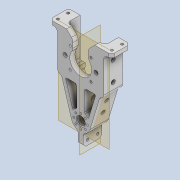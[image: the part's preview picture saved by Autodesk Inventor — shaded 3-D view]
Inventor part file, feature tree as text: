
AUTODESK INVENTOR PART (.ipt)
format: ipt  version: 2020 (Build 240168000, 168)  size: 733,696 bytes
history: native  units: mm
features: extrude x21, sketch x21, projected_geometry x17, fillet x15, thicken_offset x6, chamfer x5, mirror x4, other x4, plane x2, pattern_circular x2, reference x2
ambient origin geometry x8: Origin, YZ Plane, XZ Plane, XY Plane, X Axis, Y Axis, Z Axis, Center Point
bodies: Solid1 (feature_tree)
feature tree (99):
  extrude  "Extrusion1"  Depth=15.0mm
  extrude  "Extrusion2"  Depth=30.0mm
  extrude  "Extrusion3"  Depth=6.0mm
  extrude  "Extrusion4"  Depth=4.0mm TaperAngle=0.0deg
  extrude  "Extrusion5"  Depth=4.0mm TaperAngle=0.0deg
  extrude  "Extrusion6"  Depth=3.0mm
  extrude  "Extrusion7"  Depth=4.0mm
  plane  "Work Plane1"
  extrude  "Extrusion8"  Depth=4.0mm
  chamfer  "Chamfer1"  Distance=10.5mm
  extrude  "Extrusion9"  Depth=30.0mm
  pattern_circular  "Circular Pattern1"  Count=2  [1 undecoded]
  thicken_offset  "Thicken1"
  fillet  "Fillet1"  Radius=80.0mm
  fillet  "Fillet2"  Radius=4.0mm
  extrude  "Extrusion10"  Depth=5.0mm
  pattern_circular  "Circular Pattern2"  [2 undecoded]
  extrude  "Extrusion11"  Depth=3.0mm
  extrude  "Extrusion12"  Depth=10.0mm TaperAngle=0.0deg
  extrude  "Extrusion13"  Depth=3.0mm TaperAngle=360.0deg
  extrude  "Extrusion14"  Depth=10.0mm TaperAngle=0.0deg
  extrude  "Extrusion15"  Depth=3.0mm
  plane  "Work Plane2"
  mirror  "Mirror1"
  extrude  "Extrusion16"  Depth=3.0mm
  extrude  "Extrusion17"  Depth=10.0mm TaperAngle=0.0deg
  mirror  "Mirror2"
  extrude  "Extrusion18"  Depth=3.0mm
  mirror  "Mirror3"
  extrude  "Extrusion19"  Depth=3.0mm
  thicken_offset  "Thicken2"
  extrude  "Extrusion20"  Depth=3.0mm
  fillet  "Fillet3"  Radius=10.0mm
  fillet  "Fillet4"  Radius=6.0mm
  fillet  "Fillet5"  Radius=7.0mm
  fillet  "Fillet6"  Radius=5.0mm
  fillet  "Fillet7"  Radius=10.0mm
  fillet  "Fillet8"  Radius=10.0mm
  chamfer  "Chamfer2"  Distance=10.0mm
  fillet  "Fillet9"  Radius=3.2mm
  thicken_offset  "Thicken3"
  thicken_offset  "Thicken4"
  fillet  "Fillet10"  Radius=3.2mm
  fillet  "Fillet11"  Radius=10.0mm
  fillet  "Fillet12"  Radius=6.0mm
  fillet  "Fillet13"  Radius=14.5mm
  chamfer  "Chamfer3"  Distance=6.0mm
  fillet  "Fillet14"  Radius=14.5mm
  chamfer  "Chamfer4"  Distance=3.0mm
  fillet  "Fillet15"  Radius=4.0mm
  extrude  "Extrusion21"  Depth=3.0mm
  mirror  "Mirror4"
  thicken_offset  "Thicken5"
  thicken_offset  "Thicken6"
  chamfer  "Chamfer5"  Distance=2.0mm
  sketch  "Sketch1"  dims[d0=38.7mm d1=15.0mm]
  reference  "Reference1"
  sketch  "Sketch2"  dims[d2=30.0mm d3=30.0mm]
  sketch  "Sketch3"  dims[d4=19.35mm d5=6.0mm]
  projected_geometry  "Projected Loop1"
  sketch  "Sketch4"  dims[d6=38.7mm d7=4.0mm d8=0.0mm]
  projected_geometry  "Projected Loop2"
  sketch  "Sketch5"  dims[d9=17.0mm d10=4.0mm d11=0.0mm]
  projected_geometry  "Projected Loop3"
  sketch  "Sketch6"  dims[d12=3.0mm d13=3.0mm]
  projected_geometry  "Projected Loop4"
  sketch  "Sketch7"  dims[d14=4.0mm d15=0.0mm d16=4.0mm]
  projected_geometry  "Projected Loop5"
  sketch  "Sketch8"  dims[d17=5.0mm d18=4.0mm]
  sketch  "Sketch9"  dims[d19=5.0mm d20=10.5mm d21=0.0mm]
  projected_geometry  "Projected Loop6"
  sketch  "Sketch10"  dims[d22=14.5mm d23=30.0mm]
  projected_geometry  "Projected Loop7"
  sketch  "Sketch11"  dims[d24=3.0mm d25=0.0mm]
  projected_geometry  "Projected Loop8"
  sketch  "Sketch12"  dims[d26=3.0mm d27=0.0mm]
  reference  "Reference2"
  sketch  "Sketch13"  dims[d28=6.15mm]
  projected_geometry  "Projected Loop9"
  sketch  "Sketch14"  dims[d29=3.0mm d30=0.0mm]
  projected_geometry  "Projected Loop10"
  sketch  "Sketch15"  dims[d31=-2.5mm]
  projected_geometry  "Projected Loop11"
  sketch  "Sketch16"  dims[d32=1.0mm]
  projected_geometry  "Projected Loop12"
  projected_geometry  "Projected Loop13"
  sketch  "Sketch17"  dims[d33=9.0mm d34=0.0mm]
  projected_geometry  "Projected Loop14"
  sketch  "Sketch18"  dims[d35=1.0mm d36=2.0mm d37=45.0deg]
  projected_geometry  "Projected Loop15"
  sketch  "Sketch19"  dims[d38=1.5mm d39=20.0mm d40=0.0mm d41=80.0mm d42=360.0deg d44=4.0mm]
  projected_geometry  "Projected Loop16"
  sketch  "Sketch20"  dims[d45=4.0mm d46=5.0mm]
  sketch  "Sketch21"  dims[d47=3.0mm d48=11.5mm d49=1.8mm d50=10.0mm d51=0.0mm d52=40.0mm d53=360.0deg d55=10.0mm d56=0.0mm d57=20.0mm d58=12.0mm d59=10.0mm d60=0.0mm d61=13.0mm d62=4.0mm d63=12.0mm d64=10.0mm d65=0.0mm d66=6.0mm d67=7.0mm d68=5.0mm d69=10.0mm d70=0.0mm d71=10.0mm d72=10.0mm d73=3.2mm d74=3.2mm d75=10.0mm d76=0.0mm d77=6.0mm d78=14.5mm d79=6.0mm d80=14.5mm d81=3.0mm d82=0.0mm d83=4.0mm d84=4.0mm d85=2.0mm d86=2.0mm d87=3.0mm d88=0.0mm d89=7.0mm d90=15.0mm d91=3.2mm d92=3.2mm d93=3.0mm d94=0.0mm d95=4.0mm d96=2.0mm d97=4.0mm d98=2.0mm d99=4.0mm d100=0.0mm d101=2.0mm d102=2.0mm d103=12.0mm d104=3.2mm d105=12.0mm d106=3.2mm d107=4.0mm d108=0.0mm d109=5.0mm d110=0.5mm d111=1.0mm d112=1.0mm d113=3.0mm d114=2.0mm d115=2.0mm d116=2.0mm d117=45.0deg d118=2.0mm d119=2.0mm d120=2.0mm d121=2.0mm d122=2.0mm d123=1.5mm d124=2.0mm d125=3.0mm d126=4.0mm d127=5.0mm d128=2.0mm d129=45.0deg d130=4.0mm d131=2.0mm d132=2.0mm d133=45.0deg d134=3.0mm d135=5.0mm d136=5.0mm d137=5.0mm d138=5.0mm d139=4.0mm d140=0.0mm d141=0.07mm d142=0.07mm d143=0.07mm d144=0.07mm d145=0.5mm d146=2.0mm d147=45.0deg]
  projected_geometry  "Projected Loop17"
  parser-record x1  (decoder bookkeeping rows leaked as tree rows — omitted from the tree; the rows remain in map.json)
  other  "reducer_unit.iam"
  other  "mot_27_ass:1"
  other  "mot_27_2:1"
note: 3 required parameter values undecoded (feature->parameter linkage not recoverable at this tier; creation-order binding heuristic only, values carry confidence <= 0.55)
note: 1 file-system path scrubbed to <path> (originals preserved in map.json)
